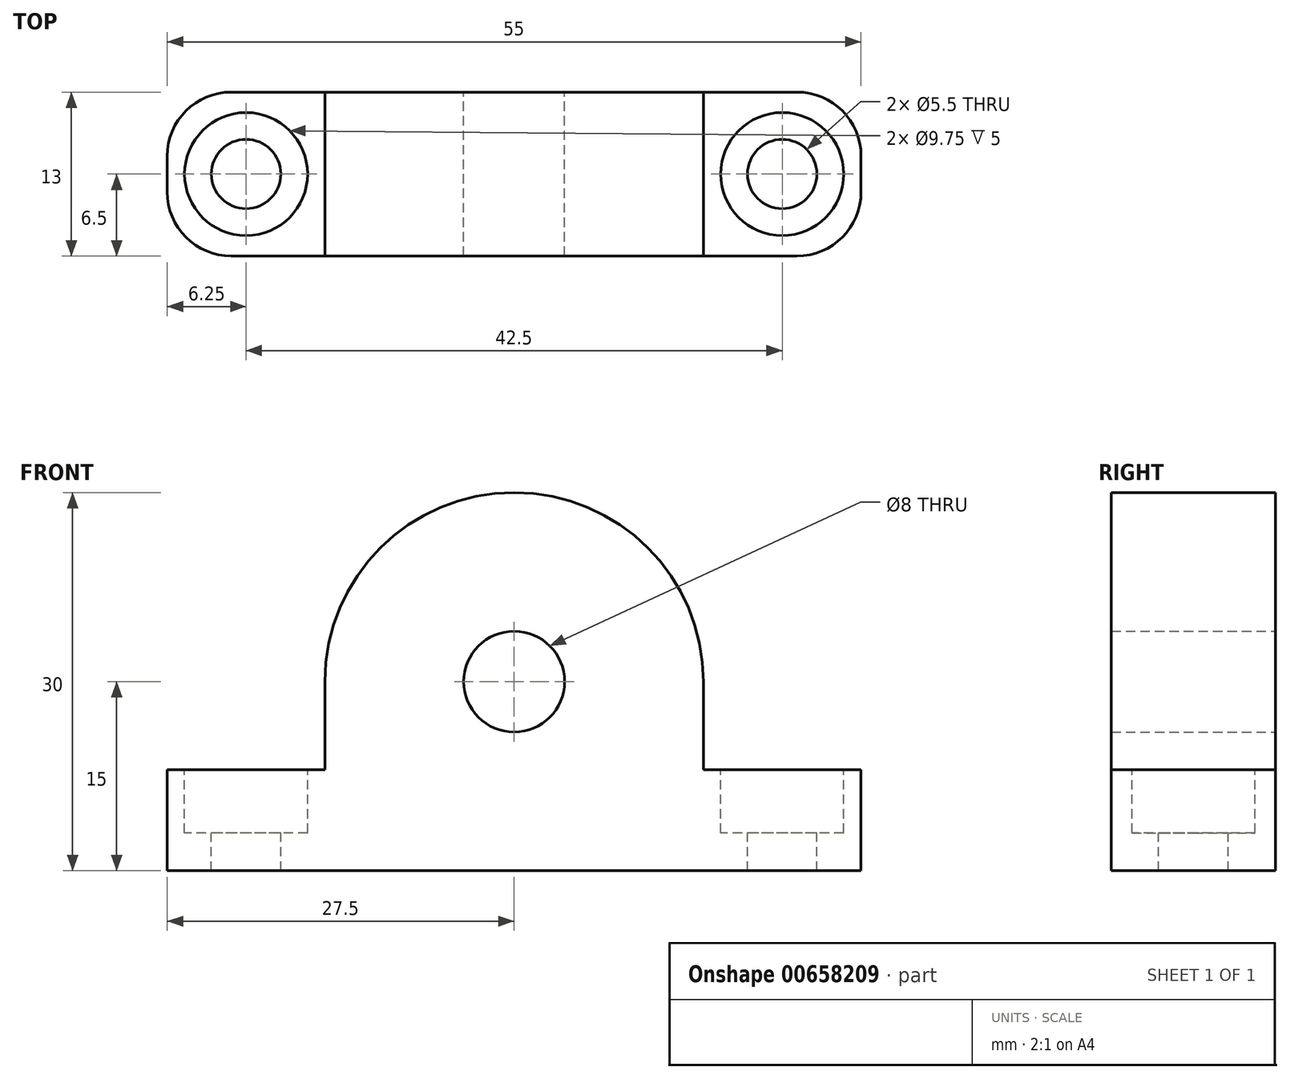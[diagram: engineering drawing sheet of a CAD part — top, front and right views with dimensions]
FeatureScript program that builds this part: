
annotation { "Feature Type Name" : "Feature", "Feature Type Description" : "" }
export const myFeature = defineFeature(function(context is Context, id is Id, definition is map)
    precondition{}
    {
        {
            var Q0;
            Q0=qCreatedBy(makeId("Front.planeOp"),FACE);
            var sketch = newSketch(context, id + "F0", { "sketchPlane" : qUnion([Q0])});
            skLineSegment(sketch, "E0", {"start": v(-27.5, 0) * mm, "end": v(27.5, 0) * mm});
            skLineSegment(sketch, "E1", {"start": v(0, 0) * mm, "end": v(0, 30) * mm, "construction": true});
            skArc(sketch, "E2", {"start": v(15, 15) * mm, "mid": v(0, 30) * mm, "end": v(-15, 15) * mm});
            skLineSegment(sketch, "E3", {"start": v(-27.5, 0) * mm, "end": v(-27.5, 8) * mm});
            skCircle(sketch, "E4", {"center": v(0, 15) * mm, "radius": 4 * mm});
            skLineSegment(sketch, "E5", {"start": v(-27.5, 8) * mm, "end": v(-15, 8) * mm});
            skLineSegment(sketch, "E6.MirrorCS", {"start": v(27.5, 8) * mm, "end": v(15, 8) * mm});
            skLineSegment(sketch, "E7.MirrorCS", {"start": v(27.5, 0) * mm, "end": v(27.5, 8) * mm});
            skLineSegment(sketch, "E8", {"start": v(15, 15) * mm, "end": v(15, 8) * mm});
            skLineSegment(sketch, "E9.MirrorCS", {"start": v(-15, 15) * mm, "end": v(-15, 8) * mm});
            skSolve(sketch);
        }
        {
            var Q0;
            Q0=makeQuery(id+"F0.imprint","IMPRINT",FACE,{"disambiguationData":[TD([[makeQuery(id+"F0.imprint","IMPRINT",EDGE,{"derivedFrom":sQuery(id+"F0.wireOp",EDGE,"E0")}),1.0]])]});
            extrude(context, id + "F1", {"entities" : qUnion([Q0]), "depth" : 13 * mm, "offsetDistance" : 25.4 * mm});
        }
        {
            var Q0;
            Q0=makeQuery(id+"F1.opExtrude","SWEPT_FACE",FACE,{"disambiguationData":[OSD([sQuery(id+"F0.wireOp",EDGE,"E6.MirrorCS")])]});
            var sketch = newSketch(context, id + "F2", { "sketchPlane" : qUnion([Q0])});
            skPoint(sketch, "E10", {"position": v(21.25, -6.5) * mm});
            skPoint(sketch, "E10.positionSnap0", {"position": v(27.5, -6.5) * mm});
            skPoint(sketch, "E10.positionSnap1", {"position": v(21.25, 0) * mm});
            skPoint(sketch, "E11.MirrorP", {"position": v(-21.25, -6.5) * mm});
            skSolve(sketch);
        }
        {
            var Q0;
            Q0=sQuery(id+"F2.wireOp",VERTEX,"E11.MirrorP");
            var Q1;
            Q1=sQuery(id+"F2.wireOp",VERTEX,"E10");
            var Q2;
            Q2=makeQuery(id+"F1.opExtrude","SWEPT_BODY",BODY,{"disambiguationData":[OSD([sQuery(id+"F0.wireOp",EDGE,"E0"),sQuery(id+"F0.wireOp",EDGE,"E2"),sQuery(id+"F0.wireOp",EDGE,"E3"),sQuery(id+"F0.wireOp",EDGE,"E4"),sQuery(id+"F0.wireOp",EDGE,"E5"),sQuery(id+"F0.wireOp",EDGE,"E6.MirrorCS"),sQuery(id+"F0.wireOp",EDGE,"E7.MirrorCS"),sQuery(id+"F0.wireOp",EDGE,"E8"),sQuery(id+"F0.wireOp",EDGE,"E9.MirrorCS")])]});
            hole(context, id + "F3", {"style" : HoleStyle.C_BORE, "endStyle" : HoleEndStyle.THROUGH, "standardTappedOrClearance" : lookupTablePath({ "standard" : "ISO", "fit" : "Normal", "size" : "M5", "type" : "Clearance" }), "standardBlindInLast" : lookupTablePath({ "fit" : "Standard", "standard" : "ISO", "size" : "M5", "type" : "Clearance" }), "holeDiameter" : 5.5 * mm, "cBoreDiameter" : 9.75 * mm, "cBoreDepth" : 5 * mm, "majorDiameter" : 6.35 * mm, "isTappedThrough" : true, "tappedDepth" : 12.7 * mm, "tapClearance" : 3, "locations" : qUnion([Q0, Q1]), "scope" : qUnion([Q2])});
        }
        {
            var Q0;
            Q0=makeQuery(id+"F1.opExtrude","CAP_EDGE",EDGE,{"disambiguationData":[OSD([sQuery(id+"F0.wireOp",EDGE,"E7.MirrorCS")])],"isStart":false});
            var Q1;
            Q1=makeQuery(id+"F1.opExtrude","CAP_EDGE",EDGE,{"disambiguationData":[OSD([sQuery(id+"F0.wireOp",EDGE,"E7.MirrorCS")])],"isStart":true});
            var Q2;
            Q2=makeQuery(id+"F1.opExtrude","CAP_EDGE",EDGE,{"disambiguationData":[OSD([sQuery(id+"F0.wireOp",EDGE,"E3")])],"isStart":false});
            var Q3;
            Q3=makeQuery(id+"F1.opExtrude","CAP_EDGE",EDGE,{"disambiguationData":[OSD([sQuery(id+"F0.wireOp",EDGE,"E3")])],"isStart":true});
            fillet(context, id + "F4", {"entities" : qUnion([Q0, Q1, Q2, Q3]), "radius" : 5.08 * mm, "tangentPropagation" : true, "allowEdgeOverflow" : false});
        }
    });
